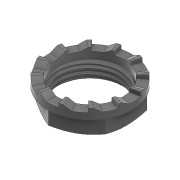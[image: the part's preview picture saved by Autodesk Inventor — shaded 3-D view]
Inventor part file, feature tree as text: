
AUTODESK INVENTOR PART (.ipt)
format: ipt  version: 2020 (Build 240168000, 168)  size: 338,944 bytes
history: native  units: in
note: dims shown in document units (in); Inventor stores cm internally (conversion verified against a paired STEP export)
features: sketch x6, extrude x3, chamfer x1, plane x1, loft x1, pattern_circular x1, thicken_offset x1, helix x1, projected_geometry x1
ambient origin geometry x8: Origin, YZ Plane, XZ Plane, XY Plane, X Axis, Y Axis, Z Axis, Center Point
bodies: Solid1 (feature_tree)
feature tree (16):
  extrude  "Extrusion1"  Depth=0.55in
  extrude  "Extrusion2"  Depth=0.125in
  chamfer  "Chamfer1"  Distance=0.085in
  extrude  "Extrusion3"  TaperAngle=0.0deg  [1 undecoded]
  sketch  "Sketch4"  dims[d8=0.02in d9=0.125in d10=45.0deg d11=0.0in d12=60.0deg]
  plane  "Work Plane1"
  loft  "Loft1"
  pattern_circular  "Circular Pattern1"  Count=12 Angle=360.0deg
  thicken_offset  "Thicken2"
  helix  "Coil1"  [1 undecoded]
  sketch  "Sketch1"  dims[d0=0.46in d1=0.55in]
  sketch  "Sketch2"  dims[d2=0.125in d3=0.0in d4=0.64in]
  sketch  "Sketch3"  dims[d5=0.5in d6=0.085in d7=0.0in]
  sketch  "Sketch5"  dims[d18=0.0in d19=90.0deg d20=0.0in d21=90.0deg d24=4.7244in d25=360.0deg d27=0.005in d28=0.002in]
  sketch  "Sketch6"  dims[d29=0.15in d30=0.09in d31=0.035in d32=60.0deg d33=0.03in d34=0.01in d35=0.155in d36=0.04in d37=0.155in d38=0.3937in d39=0.0in d40=90.0deg d41=90.0deg d42=0.0in d43=0.0in]
  projected_geometry  "Projected Loop1"
note: 2 required parameter values undecoded (feature->parameter linkage not recoverable at this tier; creation-order binding heuristic only, values carry confidence <= 0.55)
